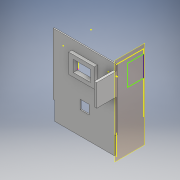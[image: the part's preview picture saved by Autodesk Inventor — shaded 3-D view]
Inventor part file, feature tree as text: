
AUTODESK INVENTOR PART (.ipt)
format: ipt  version: 2018.1 (Build 221171000, 171)  size: 438,272 bytes
history: native  units: mm
features: other x60, sketch x31, extrude x6, split x6, shell x2, chamfer x2, plane x1
ambient origin geometry x8: Origin, YZ Plane, XZ Plane, XY Plane, X Axis, Y Axis, Z Axis, Center Point
bodies: Body1 (feature_tree), Body2 (feature_tree)
feature tree (108):
  other  "Sólido1"
  extrude  "Extrusión1"  Depth=17.6mm
  sketch  "Boceto2"  dims[d2=0.9mm d3=0.0mm d6=2.4mm d7=0.0mm d8=0.9mm]
  extrude  "Extrusión2"  Depth=0.9mm TaperAngle=0.0deg
  shell  "Vaciado1"  Thickness=0.9mm
  sketch  "Boceto4"  dims[d11=3.3mm d12=8.0mm d13=0.0mm]
  sketch  "Boceto5"  dims[d14=8.0mm d15=0.0mm d16=8.0mm d17=0.0mm]
  extrude  "Extrusión3"  Depth=2.9mm
  sketch  "Boceto7"  dims[d21=2.0mm]
  sketch  "Boceto8"  dims[d22=24.5mm]
  sketch  "Boceto9"  dims[d23=7.9mm d24=10.4mm d25=0.0mm]
  sketch  "Boceto10"  dims[d26=2.0mm]
  sketch  "Boceto11"  dims[d27=2.0mm]
  sketch  "Boceto12"  dims[d28=2.9mm]
  extrude  "Extrusión4"  Depth=8.0mm TaperAngle=0.0deg
  extrude  "Extrusión5"  Depth=8.0mm TaperAngle=0.0deg
  other  "Engrosado1"
  other  "Engrosado2"
  sketch  "Boceto15"  dims[d31=0.4mm]
  extrude  "Extrusión6"  Depth=2.0mm
  other  "Engrosado3"
  other  "Engrosado4"
  other  "Engrosado5"
  other  "Engrosado6"
  other  "Engrosado7"
  shell  "Vaciado2"  Thickness=2.0mm
  other  "Engrosado8"
  other  "Engrosado9"
  other  "Engrosado10"
  other  "Engrosado11"
  other  "Engrosado12"
  other  "Engrosado13"
  other  "Engrosado14"
  other  "Engrosado15"
  other  "Engrosado16"
  sketch  "Boceto17"  dims[d33=0.4mm]
  plane  "Plano de trabajo1"
  sketch  "Boceto18"  dims[d34=0.4mm]
  sketch  "Boceto19"  dims[d35=0.4mm]
  other  "Forma1"
  split  "Dividir1"
  other  "Engrosado17"
  other  "Engrosado18"
  other  "Engrosado19"
  other  "Engrosado20"
  other  "Engrosado21"
  other  "Suprimir cara1"
  other  "Combinar1"
  other  "Engrosado22"
  other  "Engrosado23"
  chamfer  "Chaflán1"  Distance=10.4mm
  chamfer  "Chaflán2"  Distance=0.6mm
  sketch  "Boceto20"  dims[d36=0.9mm]
  sketch  "Boceto21"  dims[d37=0.4mm]
  other  "Engrosado24"
  other  "Engrosado25"
  other  "Engrosado26"
  other  "Engrosado27"
  other  "Engrosado28"
  sketch  "Boceto22"  dims[d38=0.4mm]
  split  "Dividir2"
  other  "Engrosado29"
  sketch  "Boceto24"  dims[d40=0.4mm]
  split  "Dividir3"
  other  "Engrosado30"
  other  "Engrosado31"
  other  "Engrosado32"
  other  "Engrosado33"
  other  "Engrosado34"
  other  "Engrosado35"
  other  "Engrosado36"
  other  "Engrosado37"
  sketch  "Boceto26"  dims[d42=0.9mm]
  split  "Dividir4"
  other  "Engrosado38"
  other  "Engrosado39"
  split  "Dividir5"
  sketch  "Boceto28"  dims[d44=1.5mm]
  sketch  "Boceto29"  dims[d45=0.8mm]
  sketch  "Boceto30"  dims[d46=0.8mm]
  sketch  "Boceto31"  dims[d47=0.6mm d48=0.6mm d49=0.2mm d50=0.2mm d51=0.6mm d52=0.6mm d53=0.6mm d54=0.6mm d58=0.9mm d59=0.9mm d60=0.8mm d61=0.8mm d62=0.1mm d63=0.1mm d64=0.2mm d65=0.2mm d66=0.9mm d67=0.9mm d68=1.0mm d69=1.0mm d70=1.0mm d71=1.0mm d72=0.8mm d73=2.0mm d74=45.0deg d75=0.8mm d76=2.0mm d77=45.0deg d78=10.0mm d79=10.0mm d80=3.0mm d81=3.0mm d82=0.2mm d83=0.2mm d84=2.0mm d85=2.0mm d86=0.5mm d87=0.5mm d88=0.9mm d89=0.9mm d90=0.9mm d91=0.9mm d92=13.0mm d93=13.0mm d94=3.8mm d95=3.8mm d96=0.1mm d97=0.1mm d98=0.1mm d99=0.1mm d100=5.7mm d101=5.7mm d102=0.3mm d103=0.3mm d104=0.3mm d105=0.3mm d106=2.0mm d107=11.85mm d108=1.45mm d109=1.45mm d110=2.9mm d111=5.7mm d112=3.3mm d113=2.85mm d114=5.7mm d115=0.4mm d116=0.4mm d117=0.4mm d118=0.4mm d123=0.4mm d124=0.4mm d125=1.0mm d126=1.0mm d127=0.4mm d128=0.4mm d129=0.25mm d130=0.25mm d131=0.25mm d132=0.25mm d133=0.25mm d134=0.25mm d135=0.25mm d136=0.25mm d137=0.25mm d138=0.25mm d139=0.25mm d140=0.25mm d141=0.25mm d142=0.25mm d143=0.25mm d144=0.25mm d145=0.3mm d146=0.3mm d147=3.0mm d148=3.0mm d149=0.3mm d150=0.3mm d151=1.2mm d152=1.2mm]
  split  "Dividir6"
  other  "Engrosado40"
  other  "Engrosado41"
  other  "Engrosado42"
  other  "Engrosado43"
  other  "Engrosado44"
  other  "Engrosado45"
  other  "Engrosado46"
  other  "Engrosado47"
  other  "Engrosado48"
  other  "Engrosado49"
  other  "Engrosado50"
  other  "Engrosado51"
  other  "Engrosado52"
  other  "Engrosado53"
  other  "Engrosado54"
  sketch  "Boceto1"  dims[d0=16.1mm d1=17.6mm]
  sketch  "Boceto3"  dims[d9=3.3mm d10=2.9mm]
  sketch  "Boceto6"  dims[d18=2.0mm d19=2.0mm d20=2.0mm]
  sketch  "Boceto13"  dims[d29=2.9mm]
  sketch  "Boceto14"  dims[d30=0.4mm]
  sketch  "Boceto16"  dims[d32=0.4mm]
  other  "Sólido2"
  sketch  "Boceto23"  dims[d39=0.4mm]
  sketch  "Boceto25"  dims[d41=0.9mm]
  sketch  "Boceto27"  dims[d43=1.5mm]
  other  "Sup1"
